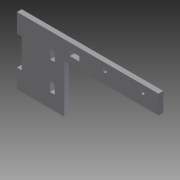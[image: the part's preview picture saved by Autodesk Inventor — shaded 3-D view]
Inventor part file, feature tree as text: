
AUTODESK INVENTOR PART (.ipt)
format: ipt  version: 2011 (Build 150239000, 239)  size: 116,736 bytes
history: native  units: in
note: dims shown in document units (in); Inventor stores cm internally (conversion verified against a paired STEP export)
features: extrude x2, sketch x2
ambient origin geometry x8: Origin, YZ Plane, XZ Plane, XY Plane, X Axis, Y Axis, Z Axis, Center Point
bodies: Solid1 (feature_tree)
feature tree (4):
  extrude  "Extrusion1"  Depth=1.0in
  extrude  "Extrusion2"  Depth=3.55in
  sketch  "Sketch2"  dims[d5=7.25in d6=1.0in]
  sketch  "Sketch3"  dims[d7=5.0in d8=3.55in d9=0.25in d10=1.0in d11=1.0in d12=0.85in d13=0.375in d14=2.0in d15=0.196in d16=0.196in d17=0.75in d18=0.75in d19=0.5in d20=0.25in d21=1.0in d22=0.25in d23=0.5in d24=0.25in d25=0.0in d26=4.2in d27=0.375in d28=0.5in d29=0.25in d30=1.0in d31=0.0in]
